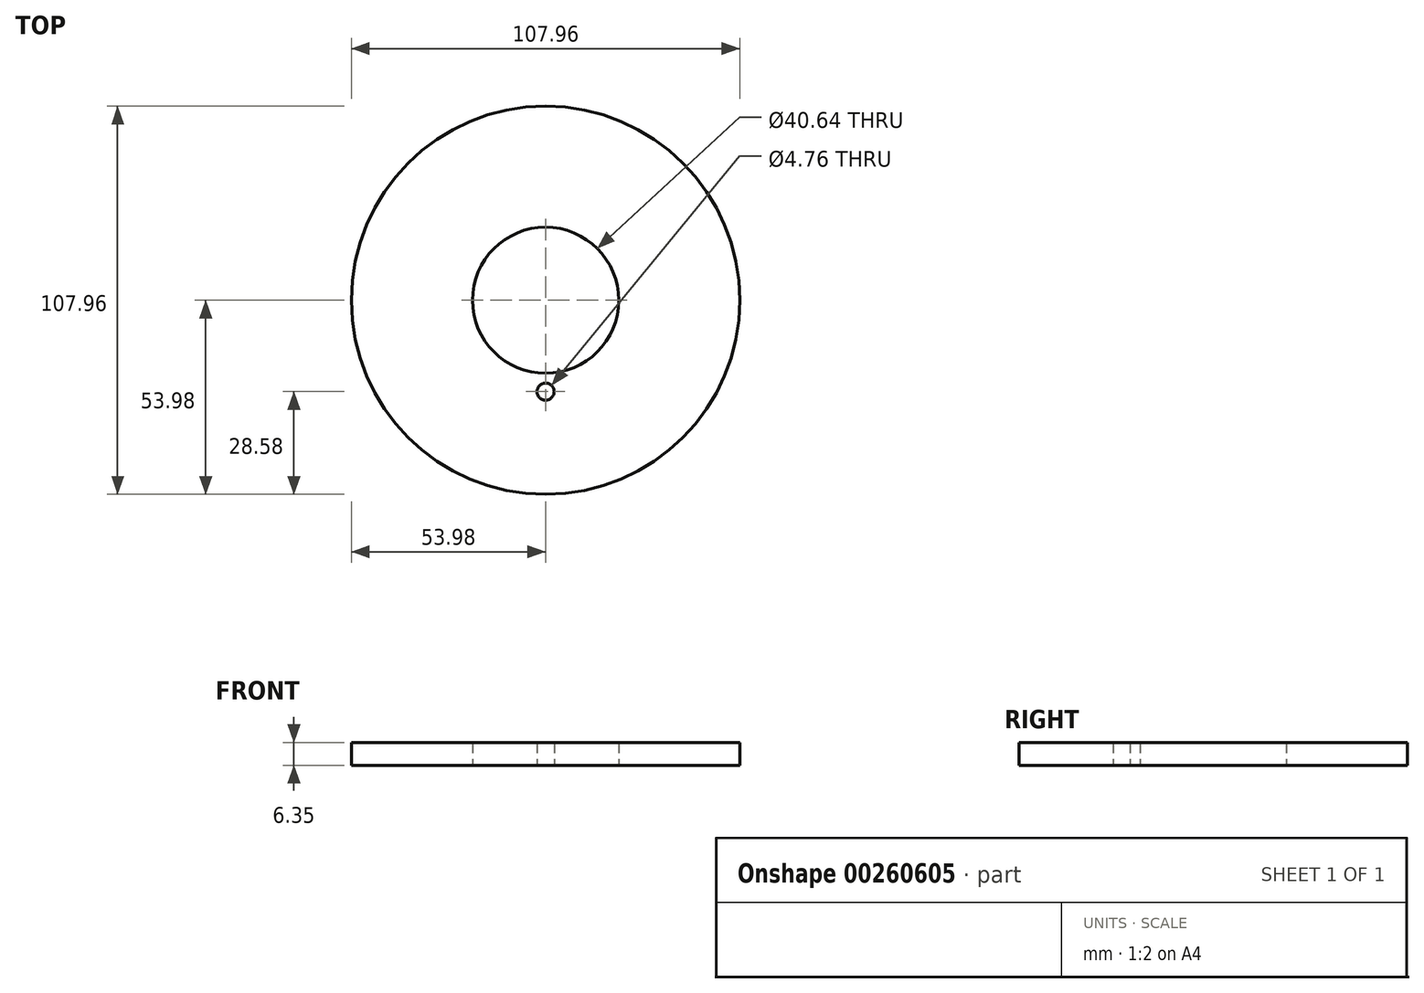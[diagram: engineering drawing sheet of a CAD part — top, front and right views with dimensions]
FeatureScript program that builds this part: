
annotation { "Feature Type Name" : "Feature", "Feature Type Description" : "" }
export const myFeature = defineFeature(function(context is Context, id is Id, definition is map)
    precondition{}
    {
        {
            var Q0;
            Q0=qCreatedBy(makeId("Top.planeOp"),FACE);
            var sketch = newSketch(context, id + "F0", { "sketchPlane" : qUnion([Q0])});
            skCircle(sketch, "E0", {"center": v(0, 0) * mm, "radius": 20.32 * mm});
            skCircle(sketch, "E1", {"center": v(0, 0) * mm, "radius": 53.98 * mm});
            skPoint(sketch, "E2", {"position": v(0, -25.4) * mm});
            skSolve(sketch);
        }
        {
            var Q0;
            Q0 = qSketchRegion(id + "F0", true);
            extrude(context, id + "F1", {"entities" : qUnion([Q0]), "depth" : 6.35 * mm});
        }
        {
            var Q0;
            Q0=sQuery(id+"F0.wireOp",VERTEX,"E2");
            var Q1;
            Q1=makeQuery(id+"F1.opExtrude","SWEPT_BODY",BODY,{"disambiguationData":[OSD([sQuery(id+"F0.wireOp",EDGE,"E0"),sQuery(id+"F0.wireOp",EDGE,"E1")])]});
            hole(context, id + "F2", {"style" : HoleStyle.SIMPLE, "endStyle" : HoleEndStyle.BLIND, "oppositeDirection" : true, "holeDiameter" : 4.76 * mm, "holeDepth" : 6.35 * mm, "tappedDepth" : 12.7 * mm, "tapClearance" : 3, "locations" : qUnion([Q0]), "scope" : qUnion([Q1])});
        }
    });
